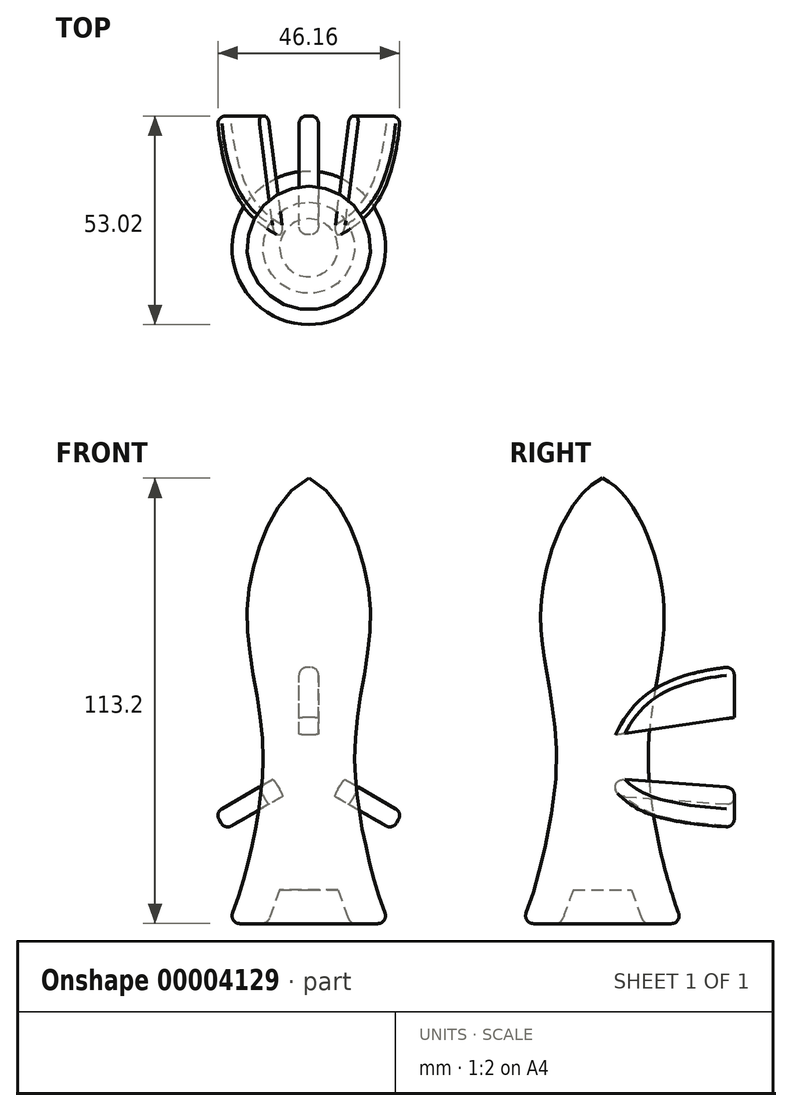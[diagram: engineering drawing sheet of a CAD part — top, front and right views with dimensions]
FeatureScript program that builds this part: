
annotation { "Feature Type Name" : "Feature", "Feature Type Description" : "" }
export const myFeature = defineFeature(function(context is Context, id is Id, definition is map)
    precondition{}
    {
        {
            var Q0;
            Q0=qCreatedBy(makeId("Right.planeOp"),FACE);
            var sketch = newSketch(context, id + "F0", { "sketchPlane" : qUnion([Q0])});
            skLineSegment(sketch, "E0", {"start": v(-74.16, 0) * mm, "end": v(19.8, 0) * mm});
            skLineSegment(sketch, "E1", {"start": v(30.43, 0) * mm, "end": v(19.8, 0) * mm});
            skFitSpline(sketch, "E2", {"points": [v(-74.16, 0) * mm, v(-42.3, 15.57) * mm, v(0, 11.71) * mm, v(39, 20.76) * mm, v(39, 21.18) * mm], "startDerivative": vector(37.44, 81.39) * mm, "endDerivative": vector(-5.84, 11.2) * mm});
            skLineSegment(sketch, "E3", {"start": v(39.06, 21.05) * mm, "end": v(39.02, 10.53) * mm});
            skLineSegment(sketch, "E4", {"start": v(39.02, 10.53) * mm, "end": v(30.43, 7.37) * mm});
            skLineSegment(sketch, "E5", {"start": v(30.43, 7.37) * mm, "end": v(30.43, 0) * mm});
            skSolve(sketch);
        }
        {
            var Q0;
            Q0=makeQuery(id+"F0.imprint","IMPRINT",FACE,{"disambiguationData":[TD([[makeQuery(id+"F0.imprint","IMPRINT",EDGE,{"derivedFrom":sQuery(id+"F0.wireOp",EDGE,"E0")}),1.0]])]});
            var Q1;
            Q1=sQuery(id+"F0.wireOp",EDGE,"E0");
            revolve(context, id + "F1", {"entities" : qUnion([Q0]), "axis" : qUnion([Q1]), "revolveType" : RevolveType.FULL});
        }
        {
            var Q0;
            Q0=qCreatedBy(makeId("Right.planeOp"),FACE);
            var sketch = newSketch(context, id + "F2", { "sketchPlane" : qUnion([Q0])});
            skLineSegment(sketch, "E6", {"start": v(33.5, 13.34) * mm, "end": v(33.5, 26.3) * mm});
            skFitSpline(sketch, "E7", {"points": [v(33.5, 26.3) * mm, v(10.56, 18.7) * mm, v(0, 0) * mm], "startDerivative": vector(-50.73, -4.98) * mm, "endDerivative": vector(-14.23, -46.2) * mm});
            skPoint(sketch, "E8.orphan", {"position": v(39, 21.18) * mm});
            skPoint(sketch, "E9.orphan", {"position": v(-74.16, 0) * mm});
            skLineSegment(sketch, "E10", {"start": v(3.32, 8.89) * mm, "end": v(33.5, 13.34) * mm});
            skSolve(sketch);
        }
        {
            var Q0;
            Q0=makeQuery(id+"F2.imprint","IMPRINT",FACE,{"disambiguationData":[TD([[makeQuery(id+"F2.imprint","IMPRINT",EDGE,{"derivedFrom":sQuery(id+"F2.wireOp",EDGE,"E6")}),1.0]])]});
            extrude(context, id + "F3", {"entities" : qUnion([Q0]), "endBound" : BoundingType.SYMMETRIC, "depth" : 5 * mm});
        }
        {
            var Q0;
            Q0=makeQuery(id+"F3.opExtrude","SWEPT_BODY",BODY,{"disambiguationData":[OSD([sQuery(id+"F2.wireOp",EDGE,"E6"),sQuery(id+"F2.wireOp",EDGE,"E7"),sQuery(id+"F2.wireOp",EDGE,"100b6dd6-4378-4da7-821a-8058ded4b564")])]});
            var Q1;
            Q1=sQuery(id+"F0.wireOp",EDGE,"E1");
            transform(context, id + "F4", {"entities" : qUnion([Q0]), "transformType" : TransformType.ROTATION, "transformAxis" : qUnion([Q1]), "angle" : 120 * degree, "makeCopy" : true});
        }
        {
            var Q0;
            Q0=makeQuery(id+"F3.opExtrude","SWEPT_BODY",BODY,{"disambiguationData":[OSD([sQuery(id+"F2.wireOp",EDGE,"E6"),sQuery(id+"F2.wireOp",EDGE,"E7"),sQuery(id+"F2.wireOp",EDGE,"100b6dd6-4378-4da7-821a-8058ded4b564")])]});
            var Q1;
            Q1=sQuery(id+"F0.wireOp",EDGE,"E1");
            transform(context, id + "F5", {"entities" : qUnion([Q0]), "transformType" : TransformType.ROTATION, "transformAxis" : qUnion([Q1]), "angle" : 120 * degree, "oppositeDirection" : true, "makeCopy" : true});
        }
        {
            var Q0;
            Q0=makeQuery(id+"F5.opPattern","COPY",EDGE,{"derivedFrom":makeQuery(id+"F3.opExtrude","SWEPT_EDGE",EDGE,{"disambiguationData":[OSD([sQuery(id+"F2.wireOp",EDGE,"E6"),sQuery(id+"F2.wireOp",EDGE,"E7")])]}),"instanceName":"1"});
            var Q1;
            Q1=makeQuery(id+"F3.opExtrude","CAP_EDGE",EDGE,{"disambiguationData":[OSD([sQuery(id+"F2.wireOp",EDGE,"E7")])],"isStart":false});
            var Q2;
            Q2=makeQuery(id+"F3.opExtrude","CAP_EDGE",EDGE,{"disambiguationData":[OSD([sQuery(id+"F2.wireOp",EDGE,"E6")])],"isStart":false});
            var Q3;
            Q3=makeQuery(id+"F4.opPattern","COPY",EDGE,{"derivedFrom":makeQuery(id+"F3.opExtrude","CAP_EDGE",EDGE,{"disambiguationData":[OSD([sQuery(id+"F2.wireOp",EDGE,"E7")])],"isStart":true}),"instanceName":"1"});
            var Q4;
            Q4=makeQuery(id+"F5.opPattern","COPY",EDGE,{"derivedFrom":makeQuery(id+"F3.opExtrude","CAP_EDGE",EDGE,{"disambiguationData":[OSD([sQuery(id+"F2.wireOp",EDGE,"E7")])],"isStart":true}),"instanceName":"1"});
            var Q5;
            Q5=makeQuery(id+"F5.opPattern","COPY",EDGE,{"derivedFrom":makeQuery(id+"F3.opExtrude","CAP_EDGE",EDGE,{"disambiguationData":[OSD([sQuery(id+"F2.wireOp",EDGE,"E7")])],"isStart":false}),"instanceName":"1"});
            var Q6;
            Q6=makeQuery(id+"F4.opPattern","COPY",EDGE,{"derivedFrom":makeQuery(id+"F3.opExtrude","CAP_EDGE",EDGE,{"disambiguationData":[OSD([sQuery(id+"F2.wireOp",EDGE,"E7")])],"isStart":false}),"instanceName":"1"});
            var Q7;
            Q7=makeQuery(id+"F4.opPattern","COPY",EDGE,{"derivedFrom":makeQuery(id+"F3.opExtrude","CAP_EDGE",EDGE,{"disambiguationData":[OSD([sQuery(id+"F2.wireOp",EDGE,"E6")])],"isStart":false}),"instanceName":"1"});
            var Q8;
            Q8=makeQuery(id+"F4.opPattern","COPY",EDGE,{"derivedFrom":makeQuery(id+"F3.opExtrude","CAP_EDGE",EDGE,{"disambiguationData":[OSD([sQuery(id+"F2.wireOp",EDGE,"E6")])],"isStart":true}),"instanceName":"1"});
            var Q9;
            Q9=makeQuery(id+"F3.opExtrude","CAP_EDGE",EDGE,{"disambiguationData":[OSD([sQuery(id+"F2.wireOp",EDGE,"E7")])],"isStart":true});
            var Q10;
            Q10=makeQuery(id+"F4.opPattern","COPY",EDGE,{"derivedFrom":makeQuery(id+"F3.opExtrude","SWEPT_EDGE",EDGE,{"disambiguationData":[OSD([sQuery(id+"F2.wireOp",EDGE,"E6"),sQuery(id+"F2.wireOp",EDGE,"E7")])]}),"instanceName":"1"});
            var Q11;
            Q11=makeQuery(id+"F5.opPattern","COPY",EDGE,{"derivedFrom":makeQuery(id+"F3.opExtrude","SWEPT_EDGE",EDGE,{"disambiguationData":[OSD([sQuery(id+"F2.wireOp",EDGE,"E6"),sQuery(id+"F2.wireOp",EDGE,"E7")])]}),"instanceName":"1"});
            var Q12;
            Q12=makeQuery(id+"F5.opPattern","COPY",EDGE,{"derivedFrom":makeQuery(id+"F3.opExtrude","CAP_EDGE",EDGE,{"disambiguationData":[OSD([sQuery(id+"F2.wireOp",EDGE,"E6")])],"isStart":false}),"instanceName":"1"});
            var Q13;
            Q13=makeQuery(id+"F5.opPattern","COPY",EDGE,{"derivedFrom":makeQuery(id+"F3.opExtrude","CAP_EDGE",EDGE,{"disambiguationData":[OSD([sQuery(id+"F2.wireOp",EDGE,"E6")])],"isStart":true}),"instanceName":"1"});
            var Q14;
            Q14=makeQuery(id+"F3.opExtrude","CAP_EDGE",EDGE,{"disambiguationData":[OSD([sQuery(id+"F2.wireOp",EDGE,"E6")])],"isStart":true});
            var Q15;
            Q15=makeQuery(id+"F4.opPattern","COPY",EDGE,{"derivedFrom":makeQuery(id+"F3.opExtrude","SWEPT_EDGE",EDGE,{"disambiguationData":[OSD([sQuery(id+"F2.wireOp",EDGE,"E6"),sQuery(id+"F2.wireOp",EDGE,"E7")])]}),"instanceName":"1"});
            var Q16;
            Q16=makeQuery(id+"F5.opPattern","COPY",EDGE,{"derivedFrom":makeQuery(id+"F3.opExtrude","SWEPT_EDGE",EDGE,{"disambiguationData":[OSD([sQuery(id+"F2.wireOp",EDGE,"E6"),sQuery(id+"F2.wireOp",EDGE,"E7")])]}),"instanceName":"1"});
            var Q17;
            Q17=makeQuery(id+"F4.opPattern","COPY",EDGE,{"derivedFrom":makeQuery(id+"F3.opExtrude","SWEPT_EDGE",EDGE,{"disambiguationData":[OSD([sQuery(id+"F2.wireOp",EDGE,"E6"),sQuery(id+"F2.wireOp",EDGE,"E7")])]}),"instanceName":"1"});
            var Q18;
            Q18=makeQuery(id+"F3.opExtrude","SWEPT_EDGE",EDGE,{"disambiguationData":[OSD([sQuery(id+"F2.wireOp",EDGE,"E6"),sQuery(id+"F2.wireOp",EDGE,"E7")])]});
            var Q19;
            Q19=makeQuery(id+"F1.opRevolve","SWEPT_EDGE",EDGE,{"disambiguationData":[OSD([sQuery(id+"F0.wireOp",EDGE,"E2"),sQuery(id+"F0.wireOp",EDGE,"E3")])]});
            var Q20;
            Q20=makeQuery(id+"F1.opRevolve","SWEPT_FACE",FACE,{"disambiguationData":[OSD([sQuery(id+"F0.wireOp",EDGE,"E3")])]});
            fillet(context, id + "F6", {"entities" : qUnion([Q0, Q1, Q2, Q3, Q4, Q5, Q6, Q7, Q8, Q9, Q10, Q11, Q12, Q13, Q14, Q15, Q16, Q17, Q18, Q19, Q20]), "radius" : 2 * mm, "tangentPropagation" : true, "allowEdgeOverflow" : false});
        }
        {
            var Q0;
            Q0=qCreatedBy(makeId("Front.planeOp"),FACE);
            var sketch = newSketch(context, id + "F7", { "sketchPlane" : qUnion([Q0])});
            skLineSegment(sketch, "E11", {"start": v(-48.75, 0) * mm, "end": v(48.26, 0) * mm});
            skSolve(sketch);
        }
        {
            var Q0;
            Q0=makeQuery(id+"F1.opRevolve","SWEPT_BODY",BODY,{"disambiguationData":[OSD([sQuery(id+"F0.wireOp",EDGE,"E0"),sQuery(id+"F0.wireOp",EDGE,"E1"),sQuery(id+"F0.wireOp",EDGE,"E2"),sQuery(id+"F0.wireOp",EDGE,"E3"),sQuery(id+"F0.wireOp",EDGE,"E4"),sQuery(id+"F0.wireOp",EDGE,"E5")])]});
            var Q1;
            Q1=sQuery(id+"F7.wireOp",EDGE,"E11");
            transform(context, id + "F8", {"entities" : qUnion([Q0]), "transformType" : TransformType.ROTATION, "transformAxis" : qUnion([Q1]), "angle" : 90 * degree, "oppositeDirection" : true, "makeCopy" : false});
        }
    });
